# Revit family: IS_Connect2_K9378_BIM_IT
name_source: partatom
category: Specialty Equipment
revit_build: Autodesk Revit 2017 (Build: 20160225_1515(x64)
units: mm (PartAtom-declared; Revit-internal decimal feet)

## family parameters
Always vertical = No
Cut with Voids When Loaded = No
OmniClass Number = 23.45.05.14.21.11
OmniClass Title = Bath/Shower Units
Part Type = Normal
Room Calculation Point = No
Round Connector Dimension = Use Diameter
Shared = No
Work Plane-Based = No

## types (1)
- K9378EO - EU 1000 WETROOM PANEL
    AltezzaNominale = 0 mm  [stored 0 ft]
    CostoDiSostituzione = 0 $
    DimensioneScarico = 0
    Installation instructions = https://www.idealspec.co.uk
    LarghezzaNominale = 0 mm  [stored 0 ft]
    LunghezzaNominale = 0 mm  [stored 0 ft]
    Maniglia = No
    Model = K9778EO
    Nominal depth = 0
    Nominal height = 0
    PiattoDoccia = No
    Product group = Quadrant Shower Enclosure
    ProfonditaNominale = 0 mm  [stored 0 ft]
    SeatMaterial = 0 mm  [stored 0 ft]
    SpessoreDelMateriale = 0
    SpilloverLivello = 0
    Uniclass 2015 Code = Pr_40_20_06_79
    Uniclass 2015 Name = Shower enclosures
    Weight Net (Kg) = 0

note: [stored X ft] marks values corroborated as IEEE doubles in the binary element streams (Revit-internal decimal feet)

## geometry (parser evidence)
native form markers: Sweep x3
no freeform markers — native parametric forms only
